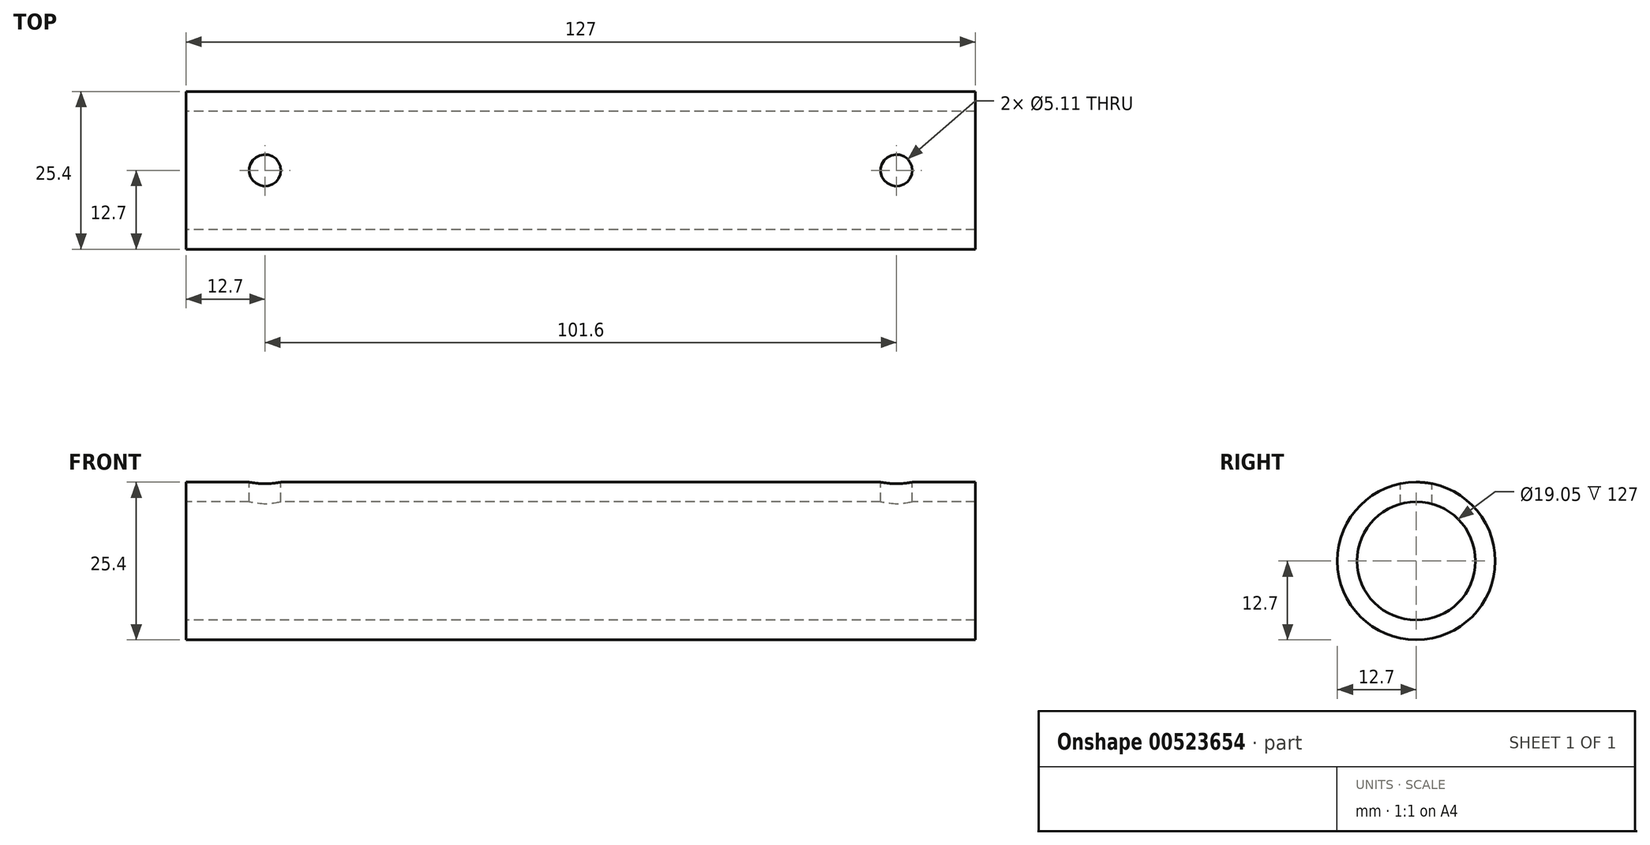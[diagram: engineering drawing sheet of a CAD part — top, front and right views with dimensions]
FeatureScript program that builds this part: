
annotation { "Feature Type Name" : "Feature", "Feature Type Description" : "" }
export const myFeature = defineFeature(function(context is Context, id is Id, definition is map)
    precondition{}
    {
        {
            var Q0;
            Q0=qCreatedBy(makeId("Right.planeOp"),FACE);
            var sketch = newSketch(context, id + "F0", { "sketchPlane" : qUnion([Q0])});
            skCircle(sketch, "E0", {"center": v(0, 0) * mm, "radius": 12.7 * mm});
            skCircle(sketch, "E1", {"center": v(0, 0) * mm, "radius": 9.53 * mm});
            skSolve(sketch);
        }
        {
            var Q0;
            Q0=makeQuery(id+"F0.imprint","IMPRINT",FACE,{"disambiguationData":[TD([[makeQuery(id+"F0.imprint","IMPRINT",EDGE,{"derivedFrom":sQuery(id+"F0.wireOp",EDGE,"E0")}),1.0]])]});
            extrude(context, id + "F1", {"entities" : qUnion([Q0]), "depth" : 127 * mm});
        }
        {
            var Q0;
            Q0=qCreatedBy(makeId("Top.planeOp"),FACE);
            cPlane(context, id + "F2", {"entities" : qUnion([Q0]), "cplaneType" : CPlaneType.OFFSET, "offset" : 12.7 * mm, "width" : 152.4 * mm, "height" : 152.4 * mm});
        }
        {
            var Q0;
            Q0=qCreatedBy(id+"F2.planeOp",FACE);
            var sketch = newSketch(context, id + "F3", { "sketchPlane" : qUnion([Q0])});
            skPoint(sketch, "E2", {"position": v(12.7, 0) * mm});
            skPoint(sketch, "E3", {"position": v(114.3, 0) * mm});
            skSolve(sketch);
        }
        {
            var Q0;
            Q0=sQuery(id+"F3.wireOp",VERTEX,"E2");
            var Q1;
            Q1=sQuery(id+"F3.wireOp",VERTEX,"E3");
            var Q2;
            Q2=makeQuery(id+"F1.opExtrude","SWEPT_BODY",BODY,{"disambiguationData":[OSD([sQuery(id+"F0.wireOp",EDGE,"E0"),sQuery(id+"F0.wireOp",EDGE,"E1")])]});
            hole(context, id + "F4", {"style" : HoleStyle.SIMPLE, "endStyle" : HoleEndStyle.BLIND, "standardTappedOrClearance" : lookupTablePath({ "standard" : "ANSI", "engagement" : "75%", "pitch" : "20 tpi", "size" : "1/4", "type" : "Tapped" }), "standardBlindInLast" : lookupTablePath({ "standard" : "ANSI", "engagement" : "75%", "pitch" : "20 tpi", "size" : "1/4", "type" : "Tapped" }), "holeDiameter" : 5.1 * mm, "showTappedDepth" : true, "holeDepth" : 12.7 * mm, "isTappedThrough" : true, "tappedDepth" : 8.9 * mm, "tapClearance" : 3, "locations" : qUnion([Q0, Q1]), "scope" : qUnion([Q2]), "majorDiameter" : 6.35 * mm});
        }
    });
